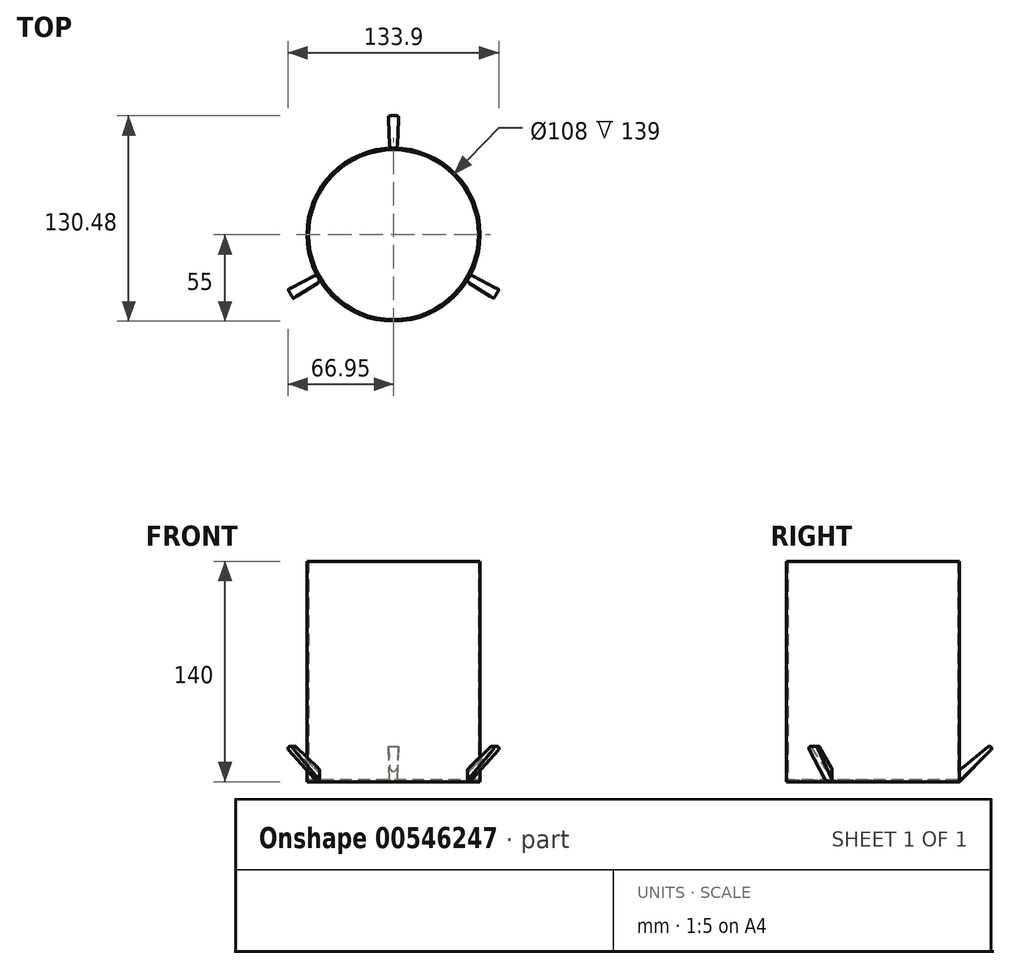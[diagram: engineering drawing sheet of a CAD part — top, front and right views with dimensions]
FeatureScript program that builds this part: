
annotation { "Feature Type Name" : "Feature", "Feature Type Description" : "" }
export const myFeature = defineFeature(function(context is Context, id is Id, definition is map)
    precondition{}
    {
        {
            var Q0;
            Q0=qCreatedBy(makeId("Top.planeOp"),FACE);
            var sketch = newSketch(context, id + "F0", { "sketchPlane" : qUnion([Q0])});
            skCircle(sketch, "E0", {"center": v(0, 0) * mm, "radius": 55 * mm});
            skSolve(sketch);
        }
        {
            var Q0;
            Q0=makeQuery(id+"F0.imprint","IMPRINT",FACE,{"disambiguationData":[TD([[makeQuery(id+"F0.imprint","IMPRINT",EDGE,{"derivedFrom":sQuery(id+"F0.wireOp",EDGE,"E0")}),1.0]])]});
            extrude(context, id + "F1", {"entities" : qUnion([Q0]), "depth" : 140 * mm, "offsetDistance" : 25 * mm});
        }
        {
            var Q0;
            Q0=makeQuery(id+"F1.opExtrude","CAP_FACE",FACE,{"disambiguationData":[OSD([sQuery(id+"F0.wireOp",EDGE,"E0")])],"isStart":false});
            shell(context, id + "F2", {"entities" : qUnion([Q0]), "thickness" : 1 * mm});
        }
        {
            var Q0;
            Q0=qCreatedBy(makeId("Right.planeOp"),FACE);
            var sketch = newSketch(context, id + "F3", { "sketchPlane" : qUnion([Q0])});
            skLineSegment(sketch, "E1", {"start": v(55, 140) * mm, "end": v(55, 0) * mm});
            skLineSegment(sketch, "E2", {"start": v(55, 0) * mm, "end": v(75.07, 20.07) * mm});
            skLineSegment(sketch, "E3", {"start": v(73.2, 22.14) * mm, "end": v(55, 7.3) * mm});
            skArc(sketch, "E4", {"start": v(75.07, 20.07) * mm, "mid": v(75.12, 22) * mm, "end": v(73.2, 22.14) * mm});
            skSolve(sketch);
        }
        {
            var Q0;
            Q0=qCreatedBy(makeId("Right.planeOp"),FACE);
            var sketch = newSketch(context, id + "F4", { "sketchPlane" : qUnion([Q0])});
            skLineSegment(sketch, "E5", {"start": v(0, -36.6) * mm, "end": v(0, 53.64) * mm});
            skSolve(sketch);
        }
        {
            var Q0;
            {var subQ0=sQuery(id+"F3.wireOp",EDGE,"E2");Q0=makeQuery(id+"F3.imprint","IMPRINT",FACE,{"disambiguationData":[TD([[makeQuery(id+"F3.imprint","IMPRINT",EDGE,{"derivedFrom":subQ0}),1.0]])]});}
            var Q1;
            Q1=sQuery(id+"F4.wireOp",EDGE,"E5");
            revolve(context, id + "F5", {"entities" : qUnion([Q0]), "axis" : qUnion([Q1]), "revolveType" : RevolveType.SYMMETRIC, "angle" : 5 * degree});
        }
        {
            var Q0;
            Q0=makeQuery(id+"F5.opRevolve","SWEPT_BODY",BODY,{"disambiguationData":[OSD([sQuery(id+"F3.wireOp",EDGE,"E1"),sQuery(id+"F3.wireOp",EDGE,"E2"),sQuery(id+"F3.wireOp",EDGE,"E3"),sQuery(id+"F3.wireOp",EDGE,"E4")])]});
            var Q1;
            Q1=sQuery(id+"F4.wireOp",EDGE,"E5");
            circularPattern(context, id + "F6", {"entities" : qUnion([Q0]), "axis" : qUnion([Q1]), "angle" : 360 * degree, "instanceCount" : 3, "equalSpace" : true});
        }
        {
            var Q0;
            Q0=makeQuery(id+"F6.opPattern","COPY",EDGE,{"derivedFrom":makeQuery(id+"F5.opRevolve","SWEPT_EDGE",EDGE,{"disambiguationData":[OSD([sQuery(id+"F3.wireOp",EDGE,"E1"),sQuery(id+"F3.wireOp",EDGE,"E3")])]}),"instanceName":"2"});
            var Q1;
            Q1=makeQuery(id+"F5.opRevolve","SWEPT_EDGE",EDGE,{"disambiguationData":[OSD([sQuery(id+"F3.wireOp",EDGE,"E1"),sQuery(id+"F3.wireOp",EDGE,"E3")])]});
            var Q2;
            Q2=makeQuery(id+"F6.opPattern","COPY",EDGE,{"derivedFrom":makeQuery(id+"F5.opRevolve","SWEPT_EDGE",EDGE,{"disambiguationData":[OSD([sQuery(id+"F3.wireOp",EDGE,"E1"),sQuery(id+"F3.wireOp",EDGE,"E3")])]}),"instanceName":"1"});
            var Q3;
            Q3=makeQuery(id+"F6.opPattern","COPY",EDGE,{"derivedFrom":makeQuery(id+"F5.opRevolve","CAP_EDGE",EDGE,{"disambiguationData":[OSD([sQuery(id+"F3.wireOp",EDGE,"E1")])],"isStart":false}),"instanceName":"1"});
            var Q4;
            Q4=makeQuery(id+"F6.opPattern","COPY",EDGE,{"derivedFrom":makeQuery(id+"F5.opRevolve","CAP_EDGE",EDGE,{"disambiguationData":[OSD([sQuery(id+"F3.wireOp",EDGE,"E1")])],"isStart":true}),"instanceName":"1"});
            var Q5;
            Q5=makeQuery(id+"F6.opPattern","COPY",EDGE,{"derivedFrom":makeQuery(id+"F5.opRevolve","CAP_EDGE",EDGE,{"disambiguationData":[OSD([sQuery(id+"F3.wireOp",EDGE,"E1")])],"isStart":true}),"instanceName":"2"});
            var Q6;
            Q6=makeQuery(id+"F6.opPattern","COPY",EDGE,{"derivedFrom":makeQuery(id+"F5.opRevolve","CAP_EDGE",EDGE,{"disambiguationData":[OSD([sQuery(id+"F3.wireOp",EDGE,"E1")])],"isStart":false}),"instanceName":"2"});
            var Q7;
            Q7=makeQuery(id+"F5.opRevolve","CAP_EDGE",EDGE,{"disambiguationData":[OSD([sQuery(id+"F3.wireOp",EDGE,"E1")])],"isStart":true});
            var Q8;
            Q8=makeQuery(id+"F5.opRevolve","CAP_EDGE",EDGE,{"disambiguationData":[OSD([sQuery(id+"F3.wireOp",EDGE,"E1")])],"isStart":false});
            fillet(context, id + "F7", {"entities" : qUnion([Q0, Q1, Q2, Q3, Q4, Q5, Q6, Q7, Q8]), "radius" : 2 * mm, "tangentPropagation" : true, "allowEdgeOverflow" : false});
        }
    });
